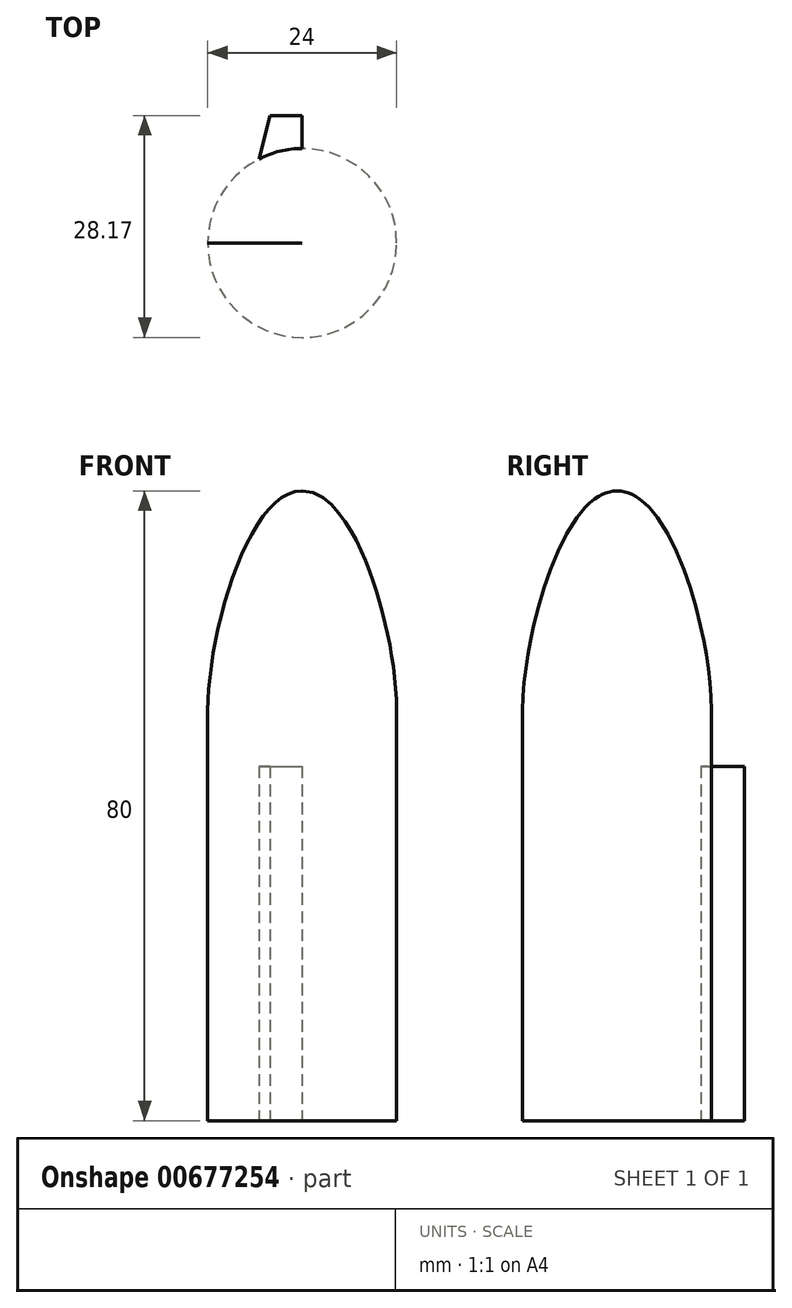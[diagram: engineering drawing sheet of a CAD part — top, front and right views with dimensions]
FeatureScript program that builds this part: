
annotation { "Feature Type Name" : "Feature", "Feature Type Description" : "" }
export const myFeature = defineFeature(function(context is Context, id is Id, definition is map)
    precondition{}
    {
        {
            var Q0;
            Q0=qCreatedBy(makeId("Front.planeOp"),FACE);
            var sketch = newSketch(context, id + "F0", { "sketchPlane" : qUnion([Q0])});
            skLineSegment(sketch, "E0.bottom", {"start": v(0, 0) * mm, "end": v(-15.49, 0) * mm});
            skLineSegment(sketch, "E0.top", {"start": v(0, 230) * mm, "end": v(-15.49, 230) * mm});
            skLineSegment(sketch, "E0.right", {"start": v(-15.49, 0) * mm, "end": v(-15.49, 230) * mm});
            skLineSegment(sketch, "E1", {"start": v(0, -32.6) * mm, "end": v(0, 270.72) * mm, "construction": true});
            skLineSegment(sketch, "E2", {"start": v(-12, 198.43) * mm, "end": v(-12, 4.08) * mm});
            skFitSpline(sketch, "E3", {"points": [v(-12, 198.43) * mm, v(0, 226.32) * mm], "startDerivative": vector(0.08, 29.32) * mm, "endDerivative": vector(20.73, -0.06) * mm});
            skLineSegment(sketch, "E4", {"start": v(0, 226.32) * mm, "end": v(0, 146.32) * mm});
            skLineSegment(sketch, "E5", {"start": v(0, 146.32) * mm, "end": v(-12, 146.32) * mm});
            skLineSegment(sketch, "E6", {"start": v(0, 196.32) * mm, "end": v(-6, 146.32) * mm});
            skLineSegment(sketch, "E7.MirrorCS", {"start": v(0, 196.32) * mm, "end": v(6, 146.32) * mm});
            skLineSegment(sketch, "E8", {"start": v(6, 146.32) * mm, "end": v(0, 146.32) * mm});
            skSolve(sketch);
        }
        {
            var Q0;
            {var subQ0=sQuery(id+"F0.wireOp",EDGE,"E3");Q0=makeQuery(id+"F0.imprint","IMPRINT",FACE,{"disambiguationData":[TD([[makeQuery(id+"F0.imprint","IMPRINT",EDGE,{"derivedFrom":subQ0}),-1.0]])]});}
            var Q1;
            {var subQ3=sQuery(id+"F0.wireOp",EDGE,"E6");Q1=makeQuery(id+"F0.imprint","IMPRINT",FACE,{"disambiguationData":[TD([[makeQuery(id+"F0.imprint","IMPRINT",EDGE,{"derivedFrom":subQ3}),1.0]])]});}
            var Q2;
            Q2=sQuery(id+"F0.wireOp",EDGE,"E1");
            revolve(context, id + "F1", {"entities" : qUnion([Q0, Q1]), "axis" : qUnion([Q2]), "revolveType" : RevolveType.FULL});
        }
        {
            var Q0;
            Q0=makeQuery(id+"F1.opRevolve","SWEPT_FACE",FACE,{"disambiguationData":[OSD([sQuery(id+"F0.wireOp",EDGE,"E5")])]});
            cPlane(context, id + "F2", {"entities" : qUnion([Q0]), "cplaneType" : CPlaneType.OFFSET, "offset" : 0 * mm, "width" : 150 * mm, "height" : 150 * mm});
        }
        {
            var Q0;
            Q0=qCreatedBy(id+"F2.planeOp",FACE);
            var sketch = newSketch(context, id + "F3", { "sketchPlane" : qUnion([Q0])});
            skLineSegment(sketch, "E9.bottom", {"start": v(0, 0) * mm, "end": v(-12, 0) * mm});
            skLineSegment(sketch, "E9.top", {"start": v(0, 12) * mm, "end": v(-12, 12) * mm});
            skLineSegment(sketch, "E9.left", {"start": v(0, 0) * mm, "end": v(0, 12) * mm});
            skLineSegment(sketch, "E9.right", {"start": v(-12, 0) * mm, "end": v(-12, 12) * mm});
            skLineSegment(sketch, "E10.bottom", {"start": v(0, 0) * mm, "end": v(12, 0) * mm});
            skLineSegment(sketch, "E10.left", {"start": v(0, 0) * mm, "end": v(0, -12) * mm});
            skLineSegment(sketch, "E10.right", {"start": v(12, 0) * mm, "end": v(12, -12) * mm});
            skCircle(sketch, "E11", {"center": v(0, 0) * mm, "radius": 12 * mm});
            skLineSegment(sketch, "E12", {"start": v(-5.5, -10.66) * mm, "end": v(-1.76, -16.17) * mm});
            skLineSegment(sketch, "E13", {"start": v(-1.76, -16.17) * mm, "end": v(0, -16.17) * mm});
            skLineSegment(sketch, "E14.MirrorCS", {"start": v(5.5, -10.66) * mm, "end": v(1.76, -16.17) * mm});
            skLineSegment(sketch, "E15", {"start": v(0, -16.17) * mm, "end": v(1.76, -16.17) * mm});
            skLineSegment(sketch, "E16", {"start": v(0, -16.17) * mm, "end": v(0, -12) * mm});
            skLineSegment(sketch, "E17", {"start": v(-4.1, -16.17) * mm, "end": v(-5.5, -10.66) * mm});
            skLineSegment(sketch, "E18", {"start": v(-4.1, -16.17) * mm, "end": v(-1.76, -16.17) * mm});
            skSolve(sketch);
        }
        {
            var Q0;
            {var subQ2=sQuery(id+"F3.wireOp",EDGE,"E12");Q0=makeQuery(id+"F3.imprint","IMPRINT",FACE,{"disambiguationData":[TD([[makeQuery(id+"F3.imprint","IMPRINT",EDGE,{"derivedFrom":subQ2}),1.0]])]});}
            var Q1;
            Q1=makeQuery(id+"F3.imprint","IMPRINT",FACE,{"disambiguationData":[TD([[makeQuery(id+"F3.imprint","IMPRINT",EDGE,{"derivedFrom":sQuery(id+"F3.wireOp",EDGE,"E12")}),-1.0]])]});
            extrude(context, id + "F4", {"entities" : qUnion([Q0, Q1]), "oppositeDirection" : true, "depth" : 45 * mm, "offsetDistance" : 25 * mm});
        }
    });
